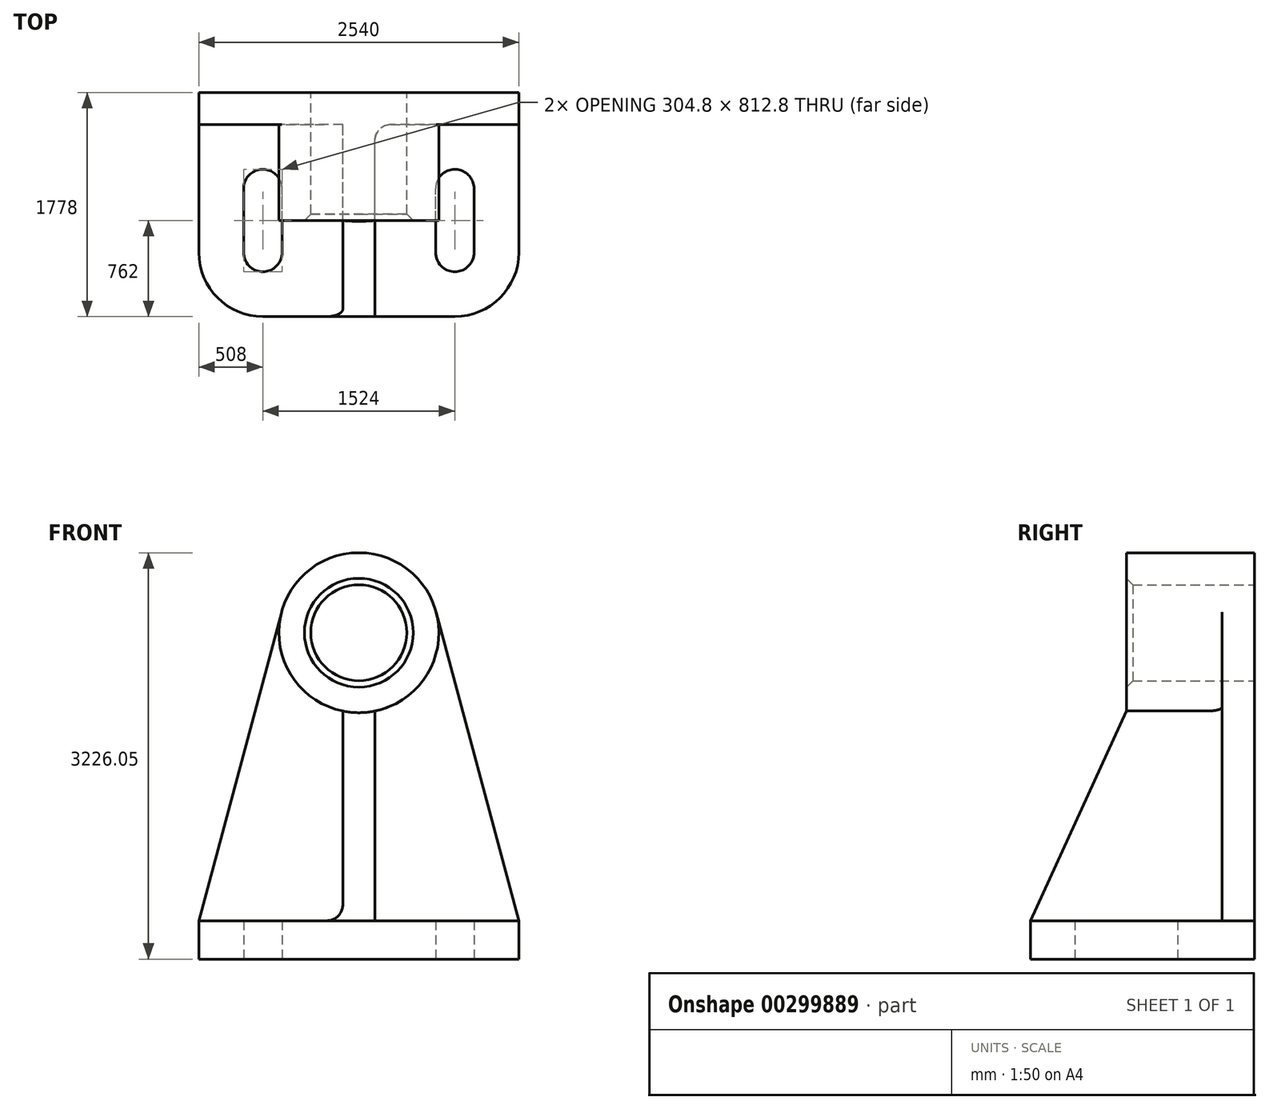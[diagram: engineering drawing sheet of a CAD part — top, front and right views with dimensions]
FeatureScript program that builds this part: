
annotation { "Feature Type Name" : "Feature", "Feature Type Description" : "" }
export const myFeature = defineFeature(function(context is Context, id is Id, definition is map)
    precondition{}
    {
        {
            var Q0;
            Q0=qCreatedBy(makeId("Top.planeOp"),FACE);
            var sketch = newSketch(context, id + "F0", { "sketchPlane" : qUnion([Q0])});
            skLineSegment(sketch, "E0.bottom", {"start": v(-1270, 0) * mm, "end": v(1270, 0) * mm});
            skLineSegment(sketch, "E0.top", {"start": v(-762, -1778) * mm, "end": v(762, -1778) * mm});
            skPoint(sketch, "E1", {"position": v(-762, -1270) * mm});
            skArc(sketch, "E2", {"start": v(-762, -1778) * mm, "mid": v(-1121.21, -1629.21) * mm, "end": v(-1270, -1270) * mm});
            skLineSegment(sketch, "E3", {"start": v(-1270, 0) * mm, "end": v(-1270, -1270) * mm});
            skArc(sketch, "E4", {"start": v(762, -1778) * mm, "mid": v(1121.21, -1629.21) * mm, "end": v(1270, -1270) * mm});
            skLineSegment(sketch, "E5", {"start": v(1270, 0) * mm, "end": v(1270, -1270) * mm});
            skLineSegment(sketch, "E6", {"start": v(-914.4, -1270) * mm, "end": v(-914.4, -762) * mm});
            skArc(sketch, "E7", {"start": v(-914.4, -1270) * mm, "mid": v(-762, -1422.4) * mm, "end": v(-609.6, -1270) * mm});
            skLineSegment(sketch, "E8", {"start": v(-609.6, -1270) * mm, "end": v(-609.6, -762) * mm});
            skArc(sketch, "E9", {"start": v(-914.4, -762) * mm, "mid": v(-762, -609.6) * mm, "end": v(-609.6, -762) * mm});
            skLineSegment(sketch, "E10", {"start": v(0, 0) * mm, "end": v(0, -184.4) * mm});
            skArc(sketch, "E11.MirrorCS", {"start": v(914.4, -762) * mm, "mid": v(762, -609.6) * mm, "end": v(609.6, -762) * mm});
            skLineSegment(sketch, "E12.MirrorCS", {"start": v(609.6, -1270) * mm, "end": v(609.6, -762) * mm});
            skLineSegment(sketch, "E13.MirrorCS", {"start": v(914.4, -1270) * mm, "end": v(914.4, -762) * mm});
            skArc(sketch, "E14.MirrorCS", {"start": v(914.4, -1270) * mm, "mid": v(762, -1422.4) * mm, "end": v(609.6, -1270) * mm});
            skSolve(sketch);
        }
        {
            var Q0;
            Q0 = qSketchRegion(id + "F0", true);
            extrude(context, id + "F1", {"entities" : qUnion([Q0]), "depth" : 304.8 * mm});
        }
        {
            var Q0;
            Q0=makeQuery(id+"F1.opExtrude","SWEPT_FACE",FACE,{"disambiguationData":[OSD([sQuery(id+"F0.wireOp",EDGE,"E0.bottom")])]});
            var sketch = newSketch(context, id + "F2", { "sketchPlane" : qUnion([Q0])});
            skPoint(sketch, "E15.endSnap0", {"position": v(0, 304.8) * mm});
            skLineSegment(sketch, "E16", {"start": v(-1270, 304.8) * mm, "end": v(1270, 304.8) * mm});
            skLineSegment(sketch, "E17", {"start": v(1270, 304.8) * mm, "end": v(613.36, 2755.4) * mm});
            skCircle(sketch, "E18", {"center": v(0, 2591.05) * mm, "radius": 635 * mm});
            skLineSegment(sketch, "E19", {"start": v(-613.36, 2755.4) * mm, "end": v(-1270, 304.8) * mm});
            skCircle(sketch, "E20", {"center": v(0, 2591.05) * mm, "radius": 381 * mm});
            skSolve(sketch);
        }
        {
            var Q0;
            Q0=makeQuery(id+"F2.imprint","IMPRINT",FACE,{"disambiguationData":[TD([[makeQuery(id+"F2.imprint","IMPRINT",EDGE,{"derivedFrom":sQuery(id+"F2.wireOp",EDGE,"E16")}),-1.0]])]});
            extrude(context, id + "F3", {"entities" : qUnion([Q0]), "operationType" : NewBodyOperationType.ADD, "oppositeDirection" : true, "depth" : 254 * mm});
        }
        {
            var Q0;
            Q0=makeQuery(id+"F2.imprint","IMPRINT",FACE,{"disambiguationData":[TD([[makeQuery(id+"F2.imprint","IMPRINT",EDGE,{"derivedFrom":sQuery(id+"F2.wireOp",EDGE,"E20")}),-1.0]])]});
            extrude(context, id + "F4", {"entities" : qUnion([Q0]), "operationType" : NewBodyOperationType.ADD, "oppositeDirection" : true, "depth" : 1016 * mm});
        }
        {
            var Q0;
            Q0=makeQuery(id+"F4.opExtrude","CAP_EDGE",EDGE,{"disambiguationData":[OSD([sQuery(id+"F2.wireOp",EDGE,"E20")])],"isStart":false});
            chamfer(context, id + "F5", {"entities" : qUnion([Q0]), "width" : 50.8 * mm, "tangentPropagation" : true});
        }
        {
            var Q0;
            Q0=makeQuery(id+"F3.opExtrude","CAP_FACE",FACE,{"disambiguationData":[OSD([sQuery(id+"F2.wireOp",EDGE,"E16"),sQuery(id+"F2.wireOp",EDGE,"E17"),sQuery(id+"F2.wireOp",EDGE,"E18"),sQuery(id+"F2.wireOp",EDGE,"E19")])],"isStart":false});
            var sketch = newSketch(context, id + "F6", { "sketchPlane" : qUnion([Q0])});
            skLineSegment(sketch, "E21.bottom", {"start": v(-127, 304.8) * mm, "end": v(127, 304.8) * mm});
            skLineSegment(sketch, "E21.left", {"start": v(-127, 304.8) * mm, "end": v(-127, 1968.88) * mm});
            skLineSegment(sketch, "E21.right", {"start": v(127, 304.8) * mm, "end": v(127, 1968.88) * mm});
            skArc(sketch, "E22", {"start": v(127, 1968.88) * mm, "mid": v(0, 1956.05) * mm, "end": v(-127, 1968.88) * mm});
            skSolve(sketch);
        }
        {
            var Q0;
            Q0 = qSketchRegion(id + "F6", true);
            extrude(context, id + "F7", {"entities" : qUnion([Q0]), "operationType" : NewBodyOperationType.ADD, "depth" : 1524 * mm});
        }
        {
            var Q0;
            Q0=makeQuery(id+"F7.opExtrude","SWEPT_FACE",FACE,{"disambiguationData":[OSD([sQuery(id+"F6.wireOp",EDGE,"E21.right")])]});
            var sketch = newSketch(context, id + "F8", { "sketchPlane" : qUnion([Q0])});
            skLineSegment(sketch, "E23", {"start": v(-1778, 304.8) * mm, "end": v(-1016, 1968.88) * mm});
            skLineSegment(sketch, "E24", {"start": v(-1778, 304.8) * mm, "end": v(-1778, 1968.88) * mm});
            skLineSegment(sketch, "E25", {"start": v(-1778, 1968.88) * mm, "end": v(-1016, 1968.88) * mm});
            skSolve(sketch);
        }
        {
            var Q0;
            Q0 = qSketchRegion(id + "F8", true);
            extrude(context, id + "F9", {"entities" : qUnion([Q0]), "operationType" : NewBodyOperationType.REMOVE, "oppositeDirection" : true, "depth" : 279.4 * mm});
        }
        {
            var Q0;
            {var subQ1=sQuery(id+"F2.wireOp",EDGE,"E16");var subQ2=sQuery(id+"F0.wireOp",EDGE,"E3");Q0=makeQuery(id+"F7.boolean.opBoolean","SPLIT",EDGE,{"disambiguationData":[TD([makeQuery(id+"F1.opExtrude","SWEPT_FACE",FACE,{"disambiguationData":[OSD([subQ2])]})])],"derivedFrom":makeQuery(id+"F3.opExtrude","CAP_EDGE",EDGE,{"disambiguationData":[OSD([subQ1])],"isStart":false})});}
            var Q1;
            Q1=makeQuery(id+"F7.opExtrude","SWEPT_EDGE",EDGE,{"disambiguationData":[OSD([sQuery(id+"F2.wireOp",EDGE,"E16"),sQuery(id+"F6.wireOp",EDGE,"E21.bottom"),sQuery(id+"F6.wireOp",EDGE,"E21.left")])]});
            var Q2;
            Q2=makeQuery(id+"F7.opExtrude","CAP_EDGE",EDGE,{"disambiguationData":[OSD([sQuery(id+"F6.wireOp",EDGE,"E21.left")])],"isStart":true});
            var Q3;
            {var subQ0=sQuery(id+"F2.wireOp",EDGE,"E18");var subQ1=sQuery(id+"F6.wireOp",EDGE,"E21.left");Q3=makeQuery(id+"F7.boolean.opBoolean","SPLIT",EDGE,{"disambiguationData":[topologyDisambiguationEdgeConnected([makeQuery(id+"F4.opExtrude","SWEPT_FACE",FACE,{"disambiguationData":[OSD([subQ0])]})])],"derivedFrom":makeQuery(id+"F7.opExtrude","SWEPT_EDGE",EDGE,{"disambiguationData":[OSD([subQ0,subQ1,sQuery(id+"F6.wireOp",EDGE,"E22")])]})});}
            var Q4;
            {var subQ0=sQuery(id+"F2.wireOp",EDGE,"E18");var subQ1=sQuery(id+"F6.wireOp",EDGE,"E21.right");Q4=makeQuery(id+"F7.boolean.opBoolean","SPLIT",EDGE,{"disambiguationData":[topologyDisambiguationEdgeConnected([makeQuery(id+"F4.opExtrude","SWEPT_FACE",FACE,{"disambiguationData":[OSD([subQ0])]})])],"derivedFrom":makeQuery(id+"F7.opExtrude","SWEPT_EDGE",EDGE,{"disambiguationData":[OSD([subQ0,subQ1,sQuery(id+"F6.wireOp",EDGE,"E22")])]})});}
            var Q5;
            Q5=makeQuery(id+"F7.opExtrude","CAP_EDGE",EDGE,{"disambiguationData":[OSD([sQuery(id+"F6.wireOp",EDGE,"E21.right")])],"isStart":true});
            var Q6;
            {var subQ1=sQuery(id+"F2.wireOp",EDGE,"E16");var subQ2=sQuery(id+"F0.wireOp",EDGE,"E5");Q6=makeQuery(id+"F7.boolean.opBoolean","SPLIT",EDGE,{"disambiguationData":[TD([makeQuery(id+"F1.opExtrude","SWEPT_FACE",FACE,{"disambiguationData":[OSD([subQ2])]})])],"derivedFrom":makeQuery(id+"F3.opExtrude","CAP_EDGE",EDGE,{"disambiguationData":[OSD([subQ1])],"isStart":false})});}
            var Q7;
            Q7=makeQuery(id+"F7.opExtrude","SWEPT_EDGE",EDGE,{"disambiguationData":[OSD([sQuery(id+"F2.wireOp",EDGE,"E16"),sQuery(id+"F6.wireOp",EDGE,"E21.bottom"),sQuery(id+"F6.wireOp",EDGE,"E21.right")])]});
            fillet(context, id + "F10", {"entities" : qUnion([Q0, Q1, Q2, Q3, Q4, Q5, Q6, Q7]), "radius" : 127 * mm, "tangentPropagation" : true, "allowEdgeOverflow" : false});
        }
    });
